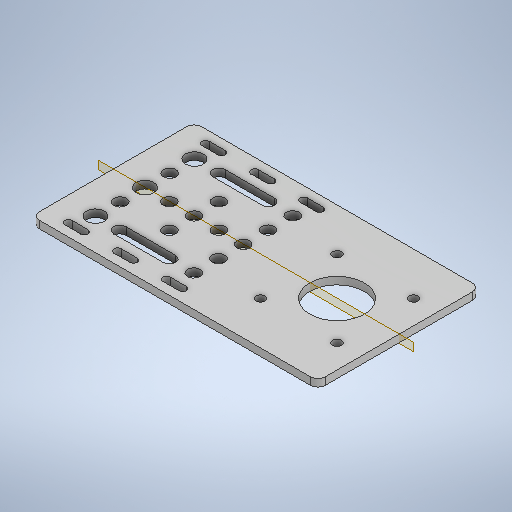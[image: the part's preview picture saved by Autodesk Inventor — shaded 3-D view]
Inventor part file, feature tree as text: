
AUTODESK INVENTOR PART (.ipt)
format: ipt  version: 2025.2 (Build 292293000, 293)  size: 344,576 bytes
history: native  units: in
note: dims shown in document units (in); Inventor stores cm internally (conversion verified against a paired STEP export)
features: extrude x2, sketch x1, fillet x1
ambient origin geometry x8: Origin, YZ Plane, XZ Plane, XY Plane, X Axis, Y Axis, Z Axis, Center Point
bodies: Solid1 (feature_tree), Body1 (feature_tree)
feature tree (4):
  sketch  "Sketch1"  dims[d0=1.9685in d1=1.7008in d2=1.7008in d3=1.2205in d4=1.2205in d5=0.8661in d6=0.1417in d7=0.1417in d8=0.1417in d9=0.1417in d10=0.1181in d11=0.0in d12=0.0in d13=0.0in d14=0.1181in]
  extrude  "Extrusion1"  Depth=0.1181in
  extrude  "Extrusion2"  Depth=0.1181in
  fillet  "Fillet1"  Radius=1.2205in
